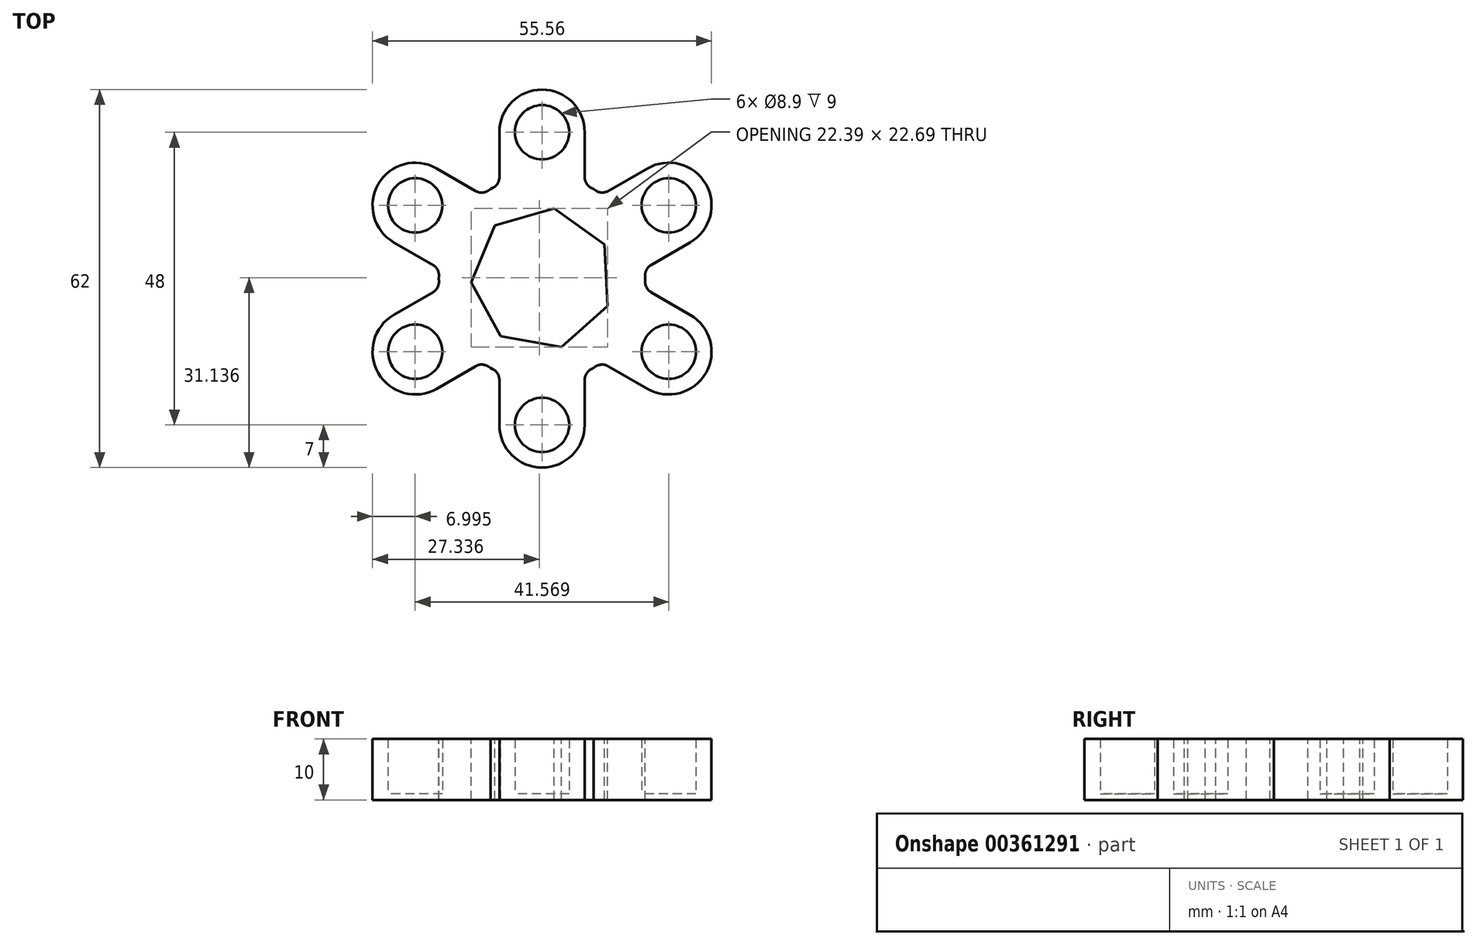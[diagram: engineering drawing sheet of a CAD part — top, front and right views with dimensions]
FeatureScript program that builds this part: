
annotation { "Feature Type Name" : "Feature", "Feature Type Description" : "" }
export const myFeature = defineFeature(function(context is Context, id is Id, definition is map)
    precondition{}
    {
        {
            var Q0;
            Q0=qCreatedBy(makeId("Top.planeOp"),FACE);
            var sketch = newSketch(context, id + "F0", { "sketchPlane" : qUnion([Q0])});
            skCircle(sketch, "E0", {"center": v(0, 0) * mm, "radius": 24 * mm, "construction": true});
            skCircle(sketch, "E1", {"center": v(0, 24) * mm, "radius": 4.45 * mm});
            skCircle(sketch, "E2", {"center": v(0, 0) * mm, "radius": 7 * mm, "construction": true});
            skArc(sketch, "E3", {"start": v(7, 24) * mm, "mid": v(0, 31) * mm, "end": v(-7, 24) * mm});
            skLineSegment(sketch, "E4", {"start": v(-27.52, 24) * mm, "end": v(41.32, 24) * mm, "construction": true});
            skLineSegment(sketch, "E5", {"start": v(-7, 24) * mm, "end": v(-7, 16.62) * mm});
            skLineSegment(sketch, "E6", {"start": v(7, 24) * mm, "end": v(7, 16.62) * mm});
            skCircle(sketch, "E7.cCircle", {"center": v(0, 0) * mm, "radius": 10.5 * mm, "construction": true});
            skLineSegment(sketch, "E7.0", {"start": v(10.75, -4.5) * mm, "end": v(3.18, -11.21) * mm});
            skLineSegment(sketch, "E7.1", {"start": v(3.18, -11.21) * mm, "end": v(-6.78, -9.48) * mm});
            skLineSegment(sketch, "E7.2", {"start": v(-6.78, -9.48) * mm, "end": v(-11.64, -0.6) * mm});
            skLineSegment(sketch, "E7.3", {"start": v(-11.64, -0.6) * mm, "end": v(-7.73, 8.72) * mm});
            skLineSegment(sketch, "E7.4", {"start": v(-7.73, 8.72) * mm, "end": v(2, 11.48) * mm});
            skLineSegment(sketch, "E7.5", {"start": v(2, 11.48) * mm, "end": v(10.22, 5.6) * mm});
            skLineSegment(sketch, "E7.6", {"start": v(10.22, 5.6) * mm, "end": v(10.75, -4.5) * mm});
            skPoint(sketch, "E7.0.midPoint", {"position": v(6.97, -7.86) * mm});
            skLineSegment(sketch, "E8", {"start": v(0, 0) * mm, "end": v(-23.99, 41.55) * mm, "construction": true});
            skLineSegment(sketch, "E9", {"start": v(0, 0) * mm, "end": v(28.24, 48.9) * mm, "construction": true});
            skArc(sketch, "E10.filletArc", {"start": v(7, 15.4) * mm, "mid": v(7, 15.4) * mm, "end": v(6.99, 15.4) * mm});
            skLineSegment(sketch, "E11.filletArc", {"start": v(-7, 15.4) * mm, "end": v(-7, 15.4) * mm});
            skCircle(sketch, "E12", {"center": v(0, 0) * mm, "radius": 16.92 * mm, "construction": true});
            skLineSegment(sketch, "E13", {"start": v(8.1, 14.84) * mm, "end": v(8.46, 14.65) * mm});
            skLineSegment(sketch, "E14", {"start": v(-8.09, 14.84) * mm, "end": v(-8.46, 14.65) * mm});
            skArc(sketch, "E15.filletArc", {"start": v(-8.09, 14.84) * mm, "mid": v(-7.3, 15.58) * mm, "end": v(-7, 16.62) * mm});
            skPoint(sketch, "E16.visualSharp", {"position": v(7, 15.4) * mm});
            skArc(sketch, "E16.filletArc", {"start": v(7, 16.62) * mm, "mid": v(7.3, 15.58) * mm, "end": v(8.1, 14.84) * mm});
            skCircle(sketch, "E17.1.0", {"center": v(-20.78, 12) * mm, "radius": 4.45 * mm});
            skLineSegment(sketch, "E17.1.1", {"start": v(-24.28, 5.94) * mm, "end": v(-17.9, 2.25) * mm});
            skLineSegment(sketch, "E17.1.2", {"start": v(-17.28, 18.06) * mm, "end": v(-10.9, 14.37) * mm});
            skArc(sketch, "E17.1.3", {"start": v(-17.28, 18.06) * mm, "mid": v(-26.85, 15.5) * mm, "end": v(-24.28, 5.94) * mm});
            skArc(sketch, "E17.1.4", {"start": v(-10.9, 14.37) * mm, "mid": v(-9.84, 14.1) * mm, "end": v(-8.8, 14.43) * mm});
            skArc(sketch, "E17.1.5", {"start": v(-16.9, 0.42) * mm, "mid": v(-17.14, 1.48) * mm, "end": v(-17.9, 2.25) * mm});
            skLineSegment(sketch, "E17.1.6", {"start": v(-8.8, 14.43) * mm, "end": v(-8.46, 14.65) * mm});
            skLineSegment(sketch, "E17.1.7", {"start": v(-16.9, 0.42) * mm, "end": v(-16.92, 0) * mm});
            skCircle(sketch, "E17.2.0", {"center": v(-20.78, -12) * mm, "radius": 4.45 * mm});
            skLineSegment(sketch, "E17.2.1", {"start": v(-17.28, -18.06) * mm, "end": v(-10.9, -14.37) * mm});
            skLineSegment(sketch, "E17.2.2", {"start": v(-24.28, -5.94) * mm, "end": v(-17.9, -2.25) * mm});
            skArc(sketch, "E17.2.3", {"start": v(-24.28, -5.94) * mm, "mid": v(-26.85, -15.5) * mm, "end": v(-17.28, -18.06) * mm});
            skArc(sketch, "E17.2.4", {"start": v(-17.9, -2.25) * mm, "mid": v(-17.14, -1.47) * mm, "end": v(-16.9, -0.41) * mm});
            skArc(sketch, "E17.2.5", {"start": v(-8.81, -14.42) * mm, "mid": v(-9.85, -14.1) * mm, "end": v(-10.9, -14.37) * mm});
            skLineSegment(sketch, "E17.2.6", {"start": v(-16.9, -0.41) * mm, "end": v(-16.92, 0) * mm});
            skLineSegment(sketch, "E17.2.7", {"start": v(-8.81, -14.42) * mm, "end": v(-8.46, -14.65) * mm});
            skCircle(sketch, "E17.3.0", {"center": v(0, -24) * mm, "radius": 4.45 * mm});
            skLineSegment(sketch, "E17.3.1", {"start": v(7, -24) * mm, "end": v(7, -16.62) * mm});
            skLineSegment(sketch, "E17.3.2", {"start": v(-7, -24) * mm, "end": v(-7, -16.62) * mm});
            skArc(sketch, "E17.3.3", {"start": v(-7, -24) * mm, "mid": v(0, -31) * mm, "end": v(7, -24) * mm});
            skArc(sketch, "E17.3.4", {"start": v(-7, -16.62) * mm, "mid": v(-7.3, -15.58) * mm, "end": v(-8.1, -14.84) * mm});
            skArc(sketch, "E17.3.5", {"start": v(8.09, -14.84) * mm, "mid": v(7.3, -15.58) * mm, "end": v(7, -16.62) * mm});
            skLineSegment(sketch, "E17.3.6", {"start": v(-8.1, -14.84) * mm, "end": v(-8.46, -14.65) * mm});
            skLineSegment(sketch, "E17.3.7", {"start": v(8.09, -14.84) * mm, "end": v(8.46, -14.65) * mm});
            skCircle(sketch, "E17.4.0", {"center": v(20.78, -12) * mm, "radius": 4.45 * mm});
            skLineSegment(sketch, "E17.4.1", {"start": v(24.28, -5.94) * mm, "end": v(17.9, -2.25) * mm});
            skLineSegment(sketch, "E17.4.2", {"start": v(17.28, -18.06) * mm, "end": v(10.9, -14.37) * mm});
            skArc(sketch, "E17.4.3", {"start": v(17.28, -18.06) * mm, "mid": v(26.85, -15.5) * mm, "end": v(24.28, -5.94) * mm});
            skArc(sketch, "E17.4.4", {"start": v(10.9, -14.37) * mm, "mid": v(9.84, -14.1) * mm, "end": v(8.8, -14.43) * mm});
            skArc(sketch, "E17.4.5", {"start": v(16.9, -0.42) * mm, "mid": v(17.14, -1.48) * mm, "end": v(17.9, -2.25) * mm});
            skLineSegment(sketch, "E17.4.6", {"start": v(8.8, -14.43) * mm, "end": v(8.46, -14.65) * mm});
            skLineSegment(sketch, "E17.4.7", {"start": v(16.9, -0.42) * mm, "end": v(16.92, 0) * mm});
            skCircle(sketch, "E17.5.0", {"center": v(20.78, 12) * mm, "radius": 4.45 * mm});
            skLineSegment(sketch, "E17.5.1", {"start": v(17.28, 18.06) * mm, "end": v(10.9, 14.37) * mm});
            skLineSegment(sketch, "E17.5.2", {"start": v(24.28, 5.94) * mm, "end": v(17.9, 2.25) * mm});
            skArc(sketch, "E17.5.3", {"start": v(24.28, 5.94) * mm, "mid": v(26.85, 15.5) * mm, "end": v(17.28, 18.06) * mm});
            skArc(sketch, "E17.5.4", {"start": v(17.9, 2.25) * mm, "mid": v(17.14, 1.47) * mm, "end": v(16.9, 0.41) * mm});
            skArc(sketch, "E17.5.5", {"start": v(8.81, 14.42) * mm, "mid": v(9.85, 14.1) * mm, "end": v(10.9, 14.37) * mm});
            skLineSegment(sketch, "E17.5.6", {"start": v(16.9, 0.41) * mm, "end": v(16.92, 0) * mm});
            skLineSegment(sketch, "E17.5.7", {"start": v(8.81, 14.42) * mm, "end": v(8.46, 14.65) * mm});
            skSolve(sketch);
        }
        {
            var Q0;
            Q0=makeQuery(id+"F0.imprint","IMPRINT",FACE,{"disambiguationData":[TD([[makeQuery(id+"F0.imprint","IMPRINT",EDGE,{"derivedFrom":sQuery(id+"F0.wireOp",EDGE,"E1")}),-1.0]])]});
            var Q1;
            Q1=makeQuery(id+"F0.imprint","IMPRINT",FACE,{"disambiguationData":[TD([[makeQuery(id+"F0.imprint","IMPRINT",EDGE,{"derivedFrom":sQuery(id+"F0.wireOp",EDGE,"E17.1.0")}),1.0]])]});
            var Q2;
            Q2=makeQuery(id+"F0.imprint","IMPRINT",FACE,{"disambiguationData":[TD([[makeQuery(id+"F0.imprint","IMPRINT",EDGE,{"derivedFrom":sQuery(id+"F0.wireOp",EDGE,"E1")}),1.0]])]});
            var Q3;
            Q3=makeQuery(id+"F0.imprint","IMPRINT",FACE,{"disambiguationData":[TD([[makeQuery(id+"F0.imprint","IMPRINT",EDGE,{"derivedFrom":sQuery(id+"F0.wireOp",EDGE,"E17.5.0")}),1.0]])]});
            var Q4;
            Q4=makeQuery(id+"F0.imprint","IMPRINT",FACE,{"disambiguationData":[TD([[makeQuery(id+"F0.imprint","IMPRINT",EDGE,{"derivedFrom":sQuery(id+"F0.wireOp",EDGE,"E17.4.0")}),1.0]])]});
            var Q5;
            Q5=makeQuery(id+"F0.imprint","IMPRINT",FACE,{"disambiguationData":[TD([[makeQuery(id+"F0.imprint","IMPRINT",EDGE,{"derivedFrom":sQuery(id+"F0.wireOp",EDGE,"E17.3.0")}),1.0]])]});
            var Q6;
            Q6=makeQuery(id+"F0.imprint","IMPRINT",FACE,{"disambiguationData":[TD([[makeQuery(id+"F0.imprint","IMPRINT",EDGE,{"derivedFrom":sQuery(id+"F0.wireOp",EDGE,"E17.2.0")}),1.0]])]});
            extrude(context, id + "F1", {"entities" : qUnion([Q0, Q1, Q2, Q3, Q4, Q5, Q6]), "oppositeDirection" : true, "depth" : 1 * mm});
        }
        {
            var Q0;
            Q0=makeQuery(id+"F0.imprint","IMPRINT",FACE,{"disambiguationData":[TD([[makeQuery(id+"F0.imprint","IMPRINT",EDGE,{"derivedFrom":sQuery(id+"F0.wireOp",EDGE,"E1")}),-1.0]])]});
            extrude(context, id + "F2", {"entities" : qUnion([Q0]), "operationType" : NewBodyOperationType.ADD, "depth" : 9 * mm});
        }
    });
